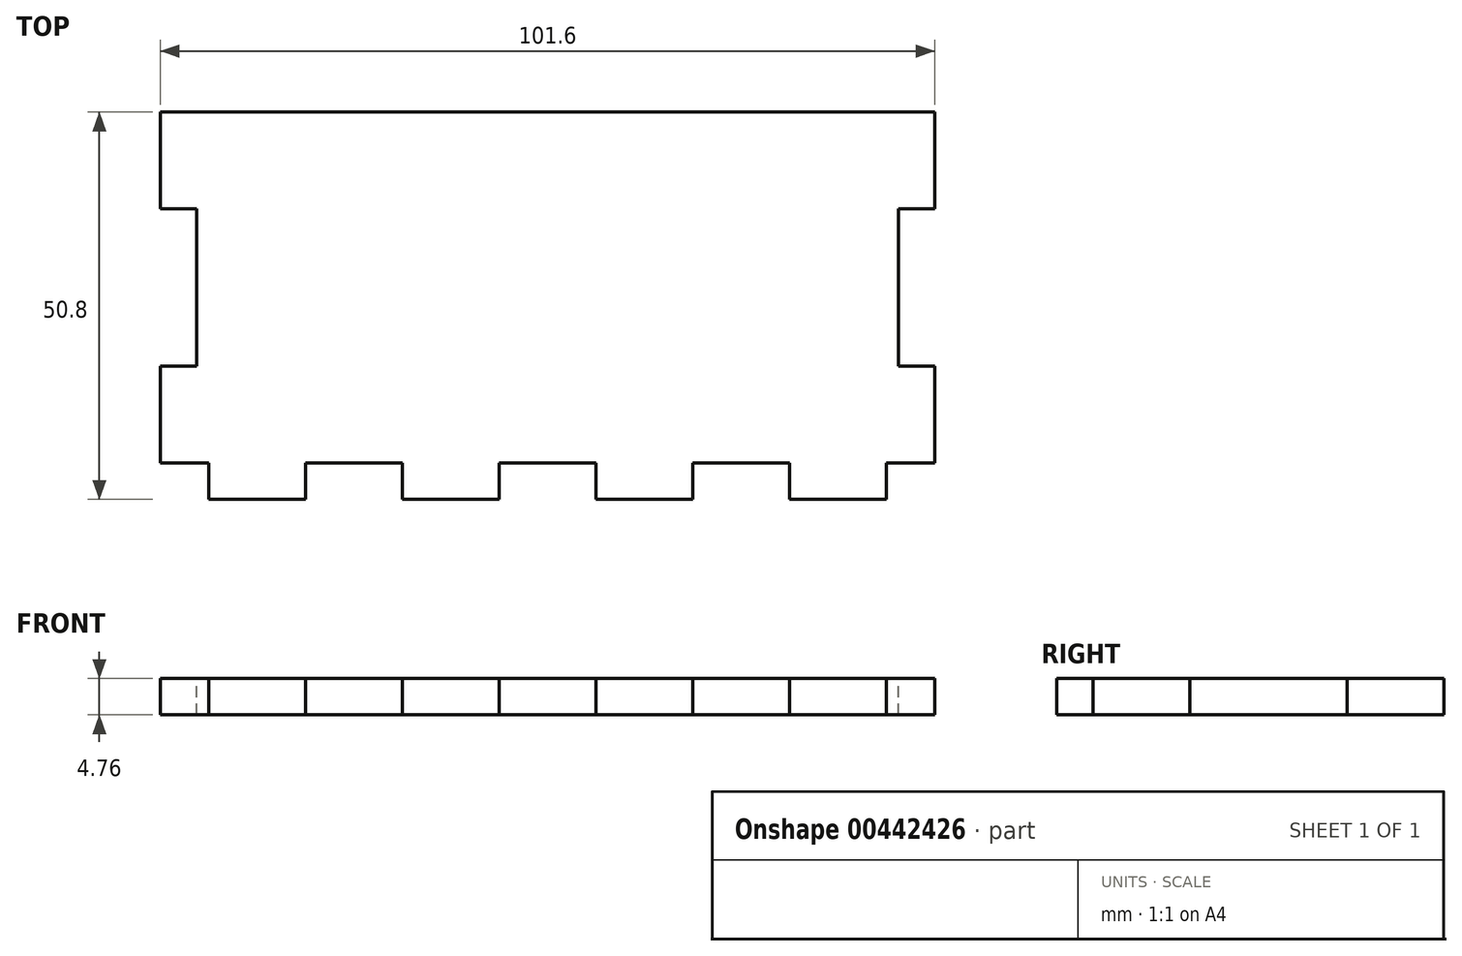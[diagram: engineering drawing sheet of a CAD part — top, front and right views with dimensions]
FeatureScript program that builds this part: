
annotation { "Feature Type Name" : "Feature", "Feature Type Description" : "" }
export const myFeature = defineFeature(function(context is Context, id is Id, definition is map)
    precondition{}
    {
        {
            var Q0;
            Q0=qCreatedBy(makeId("Top.planeOp"),FACE);
            var sketch = newSketch(context, id + "F0", { "sketchPlane" : qUnion([Q0])});
            skLineSegment(sketch, "E0.bottom", {"start": v(-50.8, 25.4) * mm, "end": v(50.8, 25.4) * mm});
            skLineSegment(sketch, "E0.top", {"start": v(-50.8, -25.4) * mm, "end": v(50.8, -25.4) * mm});
            skLineSegment(sketch, "E0.left", {"start": v(-50.8, 25.4) * mm, "end": v(-50.8, -25.4) * mm});
            skLineSegment(sketch, "E0.right", {"start": v(50.8, 25.4) * mm, "end": v(50.8, -25.4) * mm});
            skPoint(sketch, "E0.middle", {"position": v(0, 0) * mm});
            skSolve(sketch);
        }
        {
            var Q0;
            Q0 = qSketchRegion(id + "F0", true);
            extrude(context, id + "F1", {"entities" : qUnion([Q0]), "depth" : 4.76 * mm});
        }
        {
            var Q0;
            Q0=makeQuery(id+"F1.opExtrude","CAP_FACE",FACE,{"disambiguationData":[OSD([sQuery(id+"F0.wireOp",EDGE,"E0.bottom"),sQuery(id+"F0.wireOp",EDGE,"E0.top"),sQuery(id+"F0.wireOp",EDGE,"E0.left"),sQuery(id+"F0.wireOp",EDGE,"E0.right")])],"isStart":false});
            var sketch = newSketch(context, id + "F2", { "sketchPlane" : qUnion([Q0])});
            skLineSegment(sketch, "E1", {"start": v(-50.8, -25.4) * mm, "end": v(-50.8, -20.64) * mm});
            skLineSegment(sketch, "E2", {"start": v(-50.8, -20.64) * mm, "end": v(-44.45, -20.64) * mm});
            skLineSegment(sketch, "E3", {"start": v(-44.45, -20.64) * mm, "end": v(-44.45, -25.4) * mm});
            skLineSegment(sketch, "E4", {"start": v(-44.45, -25.4) * mm, "end": v(-50.8, -25.4) * mm});
            skLineSegment(sketch, "E5", {"start": v(-31.75, -25.4) * mm, "end": v(-31.75, -20.64) * mm});
            skLineSegment(sketch, "E6.1.0.0", {"start": v(-19.05, -25.4) * mm, "end": v(-19.05, -20.64) * mm});
            skLineSegment(sketch, "E6.2.0.0", {"start": v(-6.35, -25.4) * mm, "end": v(-6.35, -20.64) * mm});
            skLineSegment(sketch, "E6.3.0.0", {"start": v(6.35, -25.4) * mm, "end": v(6.35, -20.64) * mm});
            skLineSegment(sketch, "E6.4.0.0", {"start": v(19.05, -25.4) * mm, "end": v(19.05, -20.64) * mm});
            skLineSegment(sketch, "E6.direction1", {"start": v(-31.75, -25.4) * mm, "end": v(-19.05, -25.4) * mm, "construction": true});
            skLineSegment(sketch, "E7", {"start": v(-31.75, -20.64) * mm, "end": v(-19.05, -20.64) * mm});
            skLineSegment(sketch, "E8", {"start": v(-31.75, -25.4) * mm, "end": v(-19.05, -25.4) * mm});
            skLineSegment(sketch, "E9", {"start": v(-6.35, -20.64) * mm, "end": v(6.35, -20.64) * mm});
            skLineSegment(sketch, "E10", {"start": v(-6.35, -25.4) * mm, "end": v(6.35, -25.4) * mm});
            skLineSegment(sketch, "E11", {"start": v(19.05, -20.64) * mm, "end": v(31.75, -20.64) * mm});
            skLineSegment(sketch, "E12", {"start": v(50.8, -20.64) * mm, "end": v(50.8, -25.4) * mm});
            skLineSegment(sketch, "E13", {"start": v(50.8, -25.4) * mm, "end": v(44.45, -25.4) * mm});
            skLineSegment(sketch, "E14.0.5.0", {"start": v(31.75, -25.4) * mm, "end": v(31.75, -20.64) * mm});
            skLineSegment(sketch, "E15.0.6.0", {"start": v(44.45, -25.4) * mm, "end": v(44.45, -20.64) * mm});
            skLineSegment(sketch, "E16.trimOffspring", {"start": v(44.45, -20.64) * mm, "end": v(50.8, -20.64) * mm});
            skLineSegment(sketch, "E17.trimOffspring", {"start": v(31.75, -25.4) * mm, "end": v(19.05, -25.4) * mm});
            skSolve(sketch);
        }
        {
            var Q0;
            Q0 = qSketchRegion(id + "F2", true);
            extrude(context, id + "F3", {"entities" : qUnion([Q0]), "operationType" : NewBodyOperationType.REMOVE, "oppositeDirection" : true, "depth" : 25.4 * mm});
        }
        {
            var Q0;
            Q0=makeQuery(id+"F1.opExtrude","CAP_FACE",FACE,{"disambiguationData":[OSD([sQuery(id+"F0.wireOp",EDGE,"E0.bottom"),sQuery(id+"F0.wireOp",EDGE,"E0.top"),sQuery(id+"F0.wireOp",EDGE,"E0.left"),sQuery(id+"F0.wireOp",EDGE,"E0.right")])],"isStart":false});
            var sketch = newSketch(context, id + "F4", { "sketchPlane" : qUnion([Q0])});
            skLineSegment(sketch, "E18", {"start": v(-50.8, 12.7) * mm, "end": v(-46.04, 12.7) * mm});
            skLineSegment(sketch, "E19", {"start": v(-46.04, 12.7) * mm, "end": v(-46.04, -7.94) * mm});
            skLineSegment(sketch, "E20", {"start": v(-46.04, -7.94) * mm, "end": v(-50.8, -7.94) * mm});
            skLineSegment(sketch, "E21", {"start": v(-50.8, -7.94) * mm, "end": v(-50.8, 12.7) * mm});
            skLineSegment(sketch, "E22", {"start": v(0, 0) * mm, "end": v(0, 7.3) * mm, "construction": true});
            skLineSegment(sketch, "E23.MirrorCS", {"start": v(50.8, -7.94) * mm, "end": v(50.8, 12.7) * mm});
            skLineSegment(sketch, "E24.MirrorCS", {"start": v(50.8, 12.7) * mm, "end": v(46.04, 12.7) * mm});
            skLineSegment(sketch, "E25.MirrorCS", {"start": v(46.04, 12.7) * mm, "end": v(46.04, -7.94) * mm});
            skLineSegment(sketch, "E26.MirrorCS", {"start": v(46.04, -7.94) * mm, "end": v(50.8, -7.94) * mm});
            skSolve(sketch);
        }
        {
            var Q0;
            Q0 = qSketchRegion(id + "F4", true);
            extrude(context, id + "F5", {"entities" : qUnion([Q0]), "operationType" : NewBodyOperationType.REMOVE, "oppositeDirection" : true, "depth" : 25.4 * mm});
        }
    });
